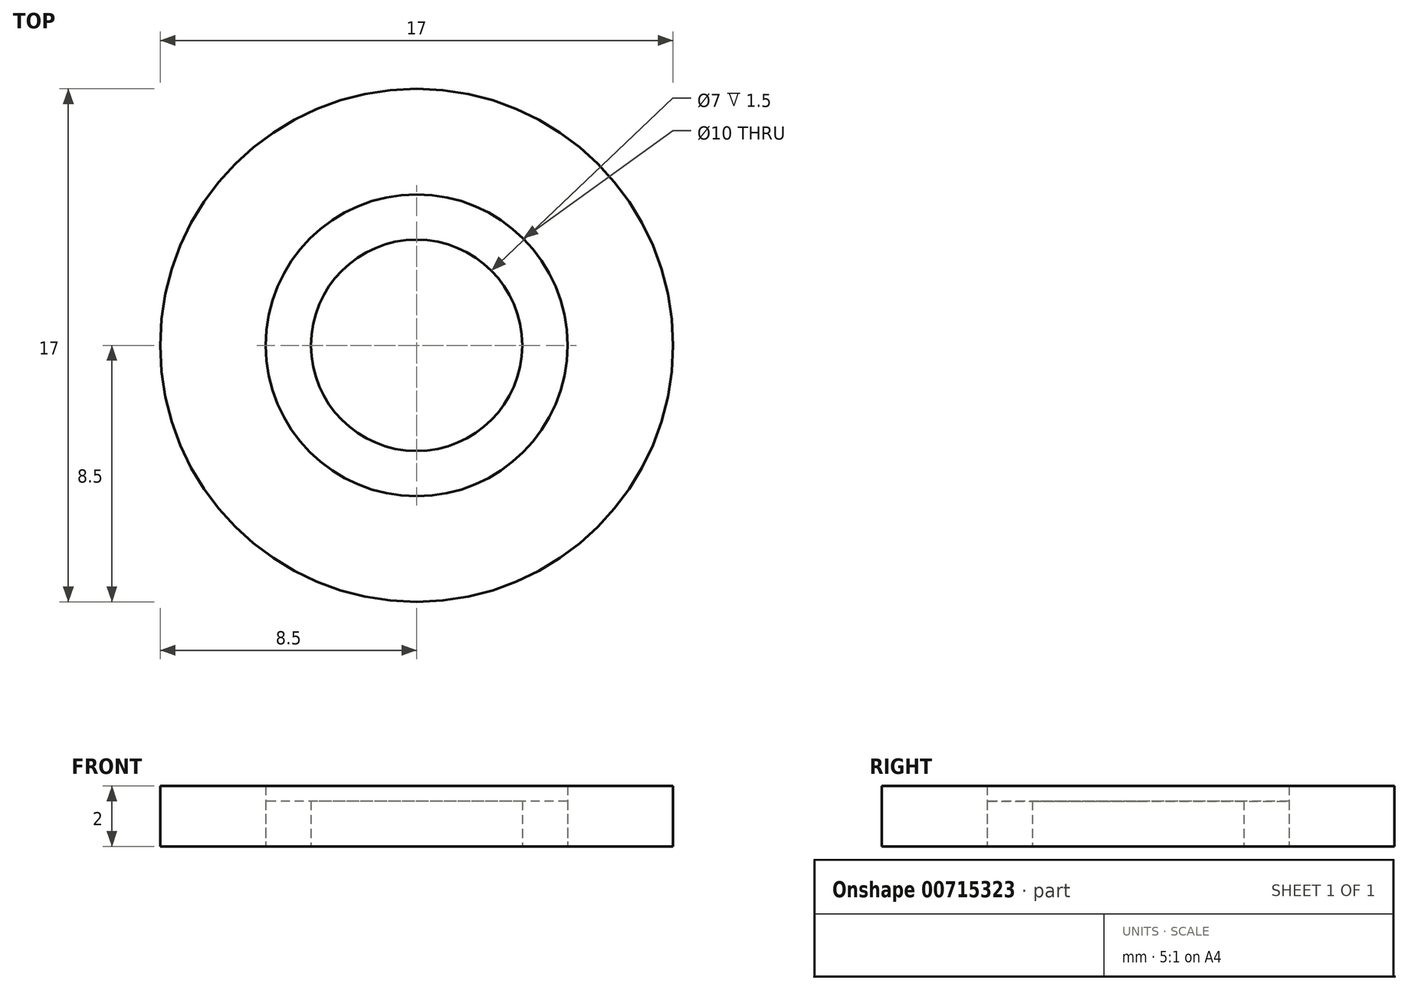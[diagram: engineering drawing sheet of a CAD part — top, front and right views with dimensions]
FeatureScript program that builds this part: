
annotation { "Feature Type Name" : "Feature", "Feature Type Description" : "" }
export const myFeature = defineFeature(function(context is Context, id is Id, definition is map)
    precondition{}
    {
        {
            var Q0;
            Q0=qCreatedBy(makeId("Top.planeOp"),FACE);
            var sketch = newSketch(context, id + "F0", { "sketchPlane" : qUnion([Q0])});
            skCircle(sketch, "E0", {"center": v(0, 0) * mm, "radius": 8.5 * mm});
            skSolve(sketch);
        }
        {
            var Q0;
            Q0=qCreatedBy(makeId("Top.planeOp"),FACE);
            var sketch = newSketch(context, id + "F1", { "sketchPlane" : qUnion([Q0])});
            skCircle(sketch, "E1", {"center": v(0, 0) * mm, "radius": 3.5 * mm});
            skSolve(sketch);
        }
        {
            var Q0;
            Q0=qCreatedBy(makeId("Top.planeOp"),FACE);
            var sketch = newSketch(context, id + "F2", { "sketchPlane" : qUnion([Q0])});
            skCircle(sketch, "E2", {"center": v(0, 0) * mm, "radius": 5 * mm});
            skSolve(sketch);
        }
        {
            var Q0;
            Q0 = qSketchRegion(id + "F0", true);
            extrude(context, id + "F3", {"entities" : qUnion([Q0]), "depth" : 2 * mm, "offsetDistance" : 25 * mm});
        }
        {
            var Q0;
            Q0 = qSketchRegion(id + "F2", true);
            extrude(context, id + "F4", {"entities" : qUnion([Q0]), "operationType" : NewBodyOperationType.REMOVE, "depth" : 5 * mm, "offsetDistance" : 25 * mm});
        }
        {
            var Q0;
            Q0 = qSketchRegion(id + "F2", true);
            extrude(context, id + "F5", {"entities" : qUnion([Q0]), "depth" : 1.5 * mm, "offsetDistance" : 25 * mm});
        }
        {
            var Q0;
            Q0 = qSketchRegion(id + "F1", true);
            extrude(context, id + "F6", {"entities" : qUnion([Q0]), "operationType" : NewBodyOperationType.REMOVE, "depth" : 25 * mm, "offsetDistance" : 25 * mm});
        }
    });
